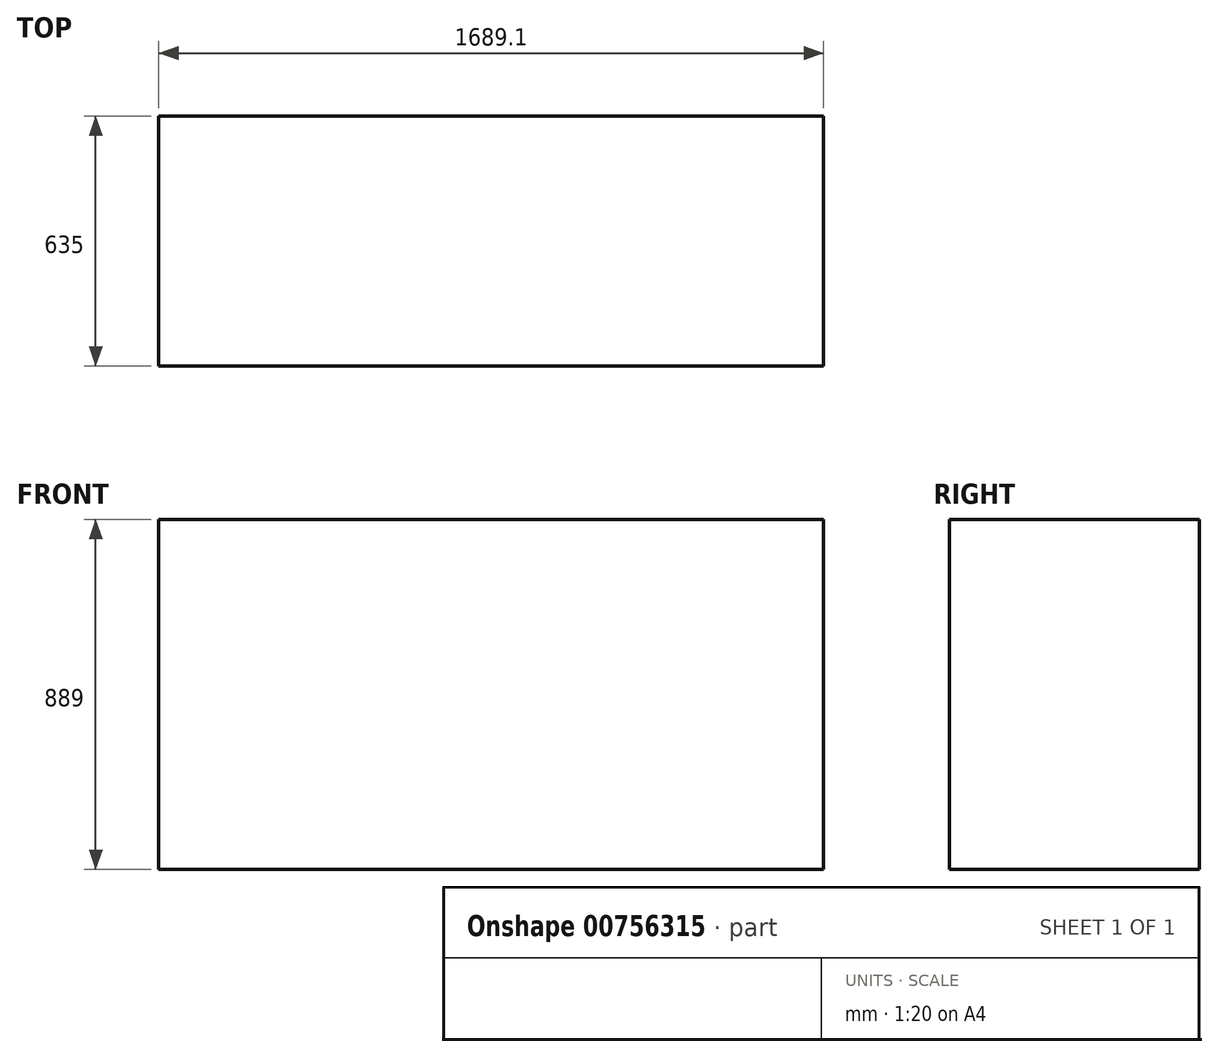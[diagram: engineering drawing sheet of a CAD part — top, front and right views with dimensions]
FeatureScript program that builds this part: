
annotation { "Feature Type Name" : "Feature", "Feature Type Description" : "" }
export const myFeature = defineFeature(function(context is Context, id is Id, definition is map)
    precondition{}
    {
        {
            var Q0;
            Q0=qCreatedBy(makeId("Top.planeOp"),FACE);
            var sketch = newSketch(context, id + "F0", { "sketchPlane" : qUnion([Q0])});
            skLineSegment(sketch, "E0.bottom", {"start": v(0, 0) * mm, "end": v(-1689.1, 0) * mm});
            skLineSegment(sketch, "E0.top", {"start": v(0, 635) * mm, "end": v(-1689.1, 635) * mm});
            skLineSegment(sketch, "E0.left", {"start": v(0, 0) * mm, "end": v(0, 635) * mm});
            skLineSegment(sketch, "E0.right", {"start": v(-1689.1, 0) * mm, "end": v(-1689.1, 635) * mm});
            skSolve(sketch);
        }
        {
            var Q0;
            Q0=makeQuery(id+"F0.imprint","IMPRINT",FACE,{"disambiguationData":[TD([[makeQuery(id+"F0.imprint","IMPRINT",EDGE,{"derivedFrom":sQuery(id+"F0.wireOp",EDGE,"E0.bottom")}),-1.0]])]});
            extrude(context, id + "F1", {"entities" : qUnion([Q0]), "oppositeDirection" : true, "depth" : 889 * mm, "offsetDistance" : 25.4 * mm});
        }
    });
